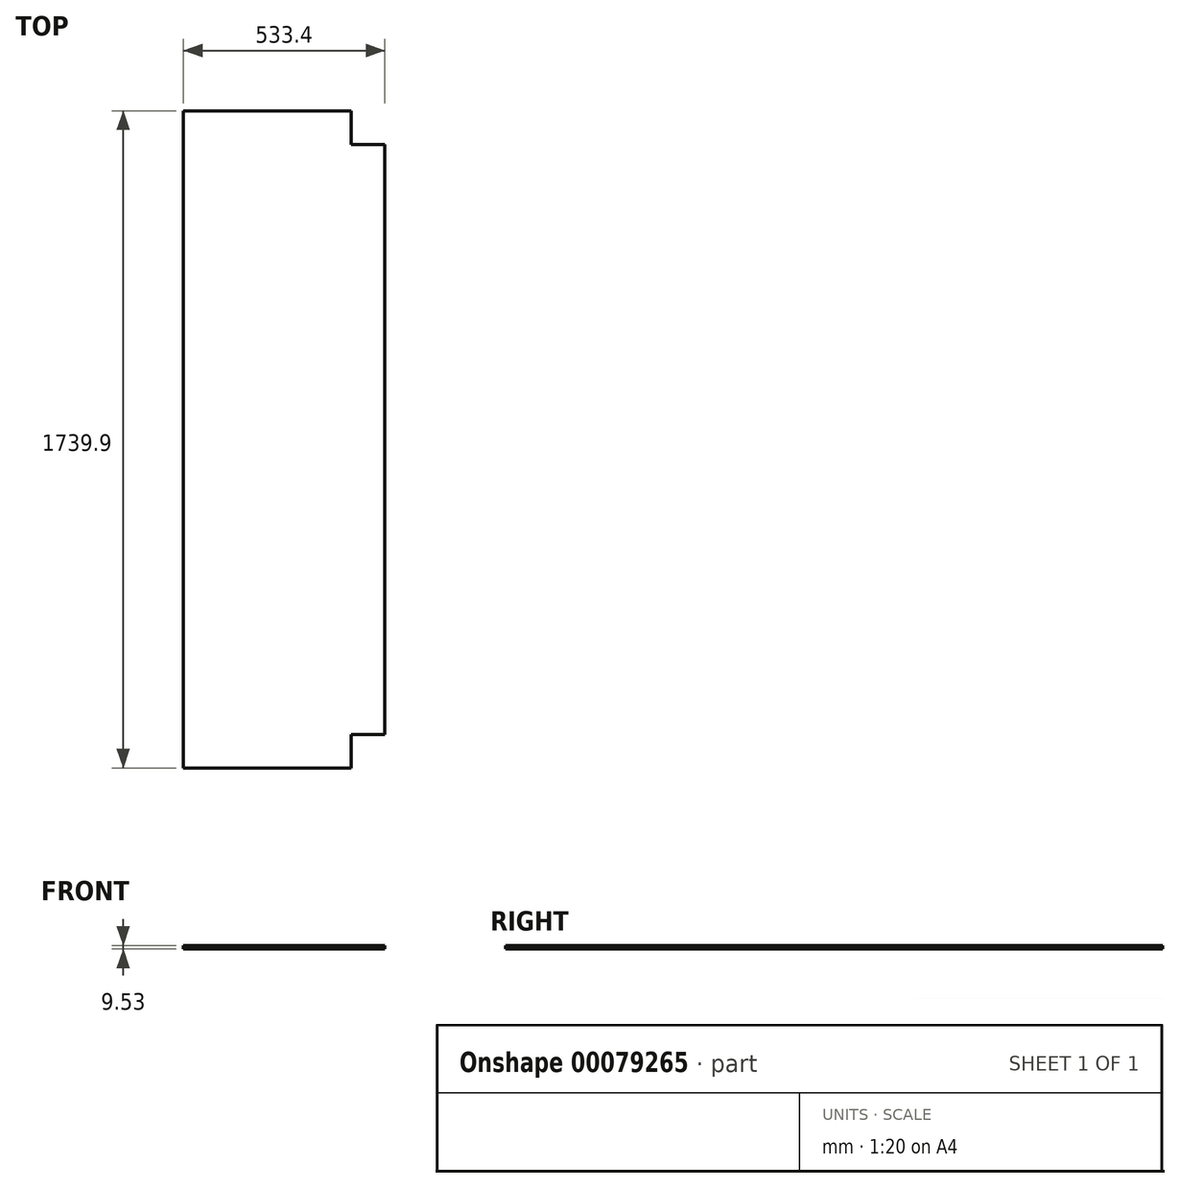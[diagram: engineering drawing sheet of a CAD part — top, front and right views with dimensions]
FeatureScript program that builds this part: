
annotation { "Feature Type Name" : "Feature", "Feature Type Description" : "" }
export const myFeature = defineFeature(function(context is Context, id is Id, definition is map)
    precondition{}
    {
        {
            var Q0;
            Q0=qCreatedBy(makeId("Top.planeOp"),FACE);
            var sketch = newSketch(context, id + "F0", { "sketchPlane" : qUnion([Q0])});
            skLineSegment(sketch, "E0", {"start": v(0, 0) * mm, "end": v(0, 1739.9) * mm});
            skLineSegment(sketch, "E1", {"start": v(0, 1739.9) * mm, "end": v(444.5, 1739.9) * mm});
            skLineSegment(sketch, "E2", {"start": v(444.5, 1739.9) * mm, "end": v(444.5, 1651) * mm});
            skLineSegment(sketch, "E3", {"start": v(444.5, 1651) * mm, "end": v(533.4, 1651) * mm});
            skLineSegment(sketch, "E4", {"start": v(533.4, 1651) * mm, "end": v(533.4, 88.9) * mm});
            skLineSegment(sketch, "E5", {"start": v(533.4, 88.9) * mm, "end": v(444.5, 88.9) * mm});
            skLineSegment(sketch, "E6", {"start": v(444.5, 88.9) * mm, "end": v(444.5, 0) * mm});
            skLineSegment(sketch, "E7", {"start": v(444.5, 0) * mm, "end": v(0, 0) * mm});
            skSolve(sketch);
        }
        {
            var Q0;
            Q0=makeQuery(id+"F0.imprint","IMPRINT",FACE,{"disambiguationData":[TD([[makeQuery(id+"F0.imprint","IMPRINT",EDGE,{"derivedFrom":sQuery(id+"F0.wireOp",EDGE,"E0")}),-1.0]])]});
            extrude(context, id + "F1", {"entities" : qUnion([Q0]), "depth" : 9.52 * mm});
        }
    });
